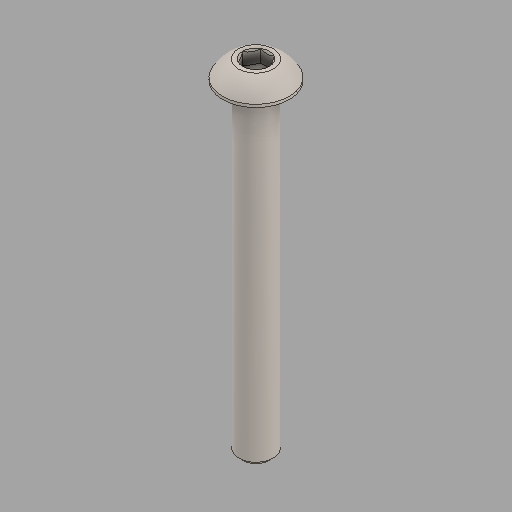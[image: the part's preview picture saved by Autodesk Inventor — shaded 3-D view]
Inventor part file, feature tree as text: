
AUTODESK INVENTOR PART (.ipt)
format: ipt  version: 2024.2 (Build 282272000, 272)  size: 111,616 bytes
history: native  units: in
note: dims shown in document units (in); Inventor stores cm internally (conversion verified against a paired STEP export)
features: fillet x1
ambient origin geometry x8: Origin, YZ Plane, XZ Plane, XY Plane, X Axis, Y Axis, Z Axis, Center Point
bodies: Solid1 (feature_tree)
feature tree (1):
  fillet  "Fillet1"  [1 undecoded]
note: 1 required parameter value undecoded (feature->parameter linkage not recoverable at this tier; creation-order binding heuristic only, values carry confidence <= 0.55)
